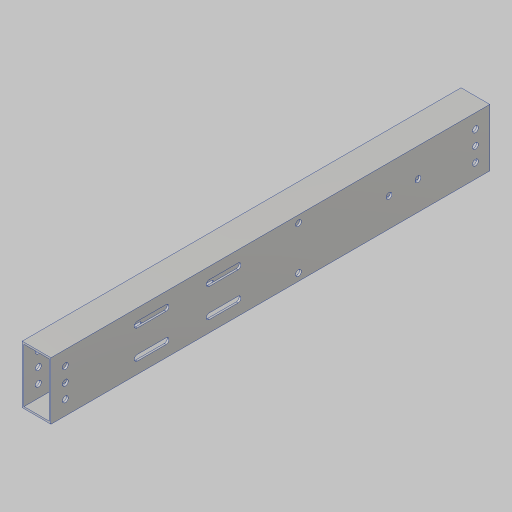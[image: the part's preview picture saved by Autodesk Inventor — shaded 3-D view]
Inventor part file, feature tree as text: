
AUTODESK INVENTOR PART (.ipt)
format: ipt  version: 2023.5 (Build 275446000, 446)  size: 194,560 bytes
history: native  units: in
note: dims shown in document units (in); Inventor stores cm internally (conversion verified against a paired STEP export)
features: sketch x4, hole x3, projected_geometry x3, extrude x2, mirror x1
ambient origin geometry x8: Origin, YZ Plane, XZ Plane, XY Plane, X Axis, Y Axis, Z Axis, Center Point
bodies: Solid1 (feature_tree)
feature tree (13):
  extrude  "Extrusion1"  Depth=0.5in
  hole  "Hole1"  [1 undecoded]
  mirror  "Mirror1"
  hole  "Hole2"  [1 undecoded]
  extrude  "Extrusion2"  Depth=0.201in
  hole  "Hole3"  [1 undecoded]
  sketch  "Sketch2"  dims[d4=0.0in d5=0.5in]
  sketch  "Sketch3"  dims[d6=0.5in d7=0.5in]
  sketch  "Sketch4"  dims[d8=0.201in d9=0.75in d10=0.385in d11=0.25in d12=0.5635in d13=1.0in d14=0.8108in d15=2.0in]
  sketch  "Sketch5"  dims[d16=1.0in d17=0.201in d18=0.38in d19=0.385in d20=0.25in d21=0.5635in d22=1.0in d23=0.8108in d25=0.201in d26=1.0in d27=1.0in d28=6.0in d29=0.201in d30=1.0in d31=1.0in d32=2.5in d33=0.0in d34=0.0in d35=1.5in d36=2.0in d37=0.201in d38=0.75in d39=0.385in d40=0.25in d41=0.5635in d42=1.0in d43=0.8108in]
  projected_geometry  "Project Cut Edges1"
  projected_geometry  "Project Cut Edges2"
  projected_geometry  "Project Cut Edges3"
note: 3 required parameter values undecoded (feature->parameter linkage not recoverable at this tier; creation-order binding heuristic only, values carry confidence <= 0.55)
